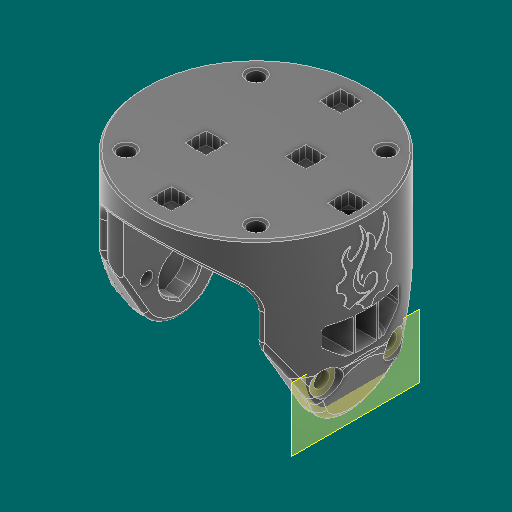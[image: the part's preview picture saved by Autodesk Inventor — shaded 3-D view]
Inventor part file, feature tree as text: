
AUTODESK INVENTOR PART (.ipt)
format: ipt  version: 2023.1 (Build 271208000, 208)  size: 2,006,016 bytes
history: native  units: in
note: dims shown in document units (in); Inventor stores cm internally (conversion verified against a paired STEP export)
features: sketch x14, other x12, plane x5
ambient origin geometry x8: Origin, YZ Plane, XZ Plane, XY Plane, X Axis, Y Axis, Z Axis, Center Point
bodies: Solid5 (feature_tree)
feature tree (31):
  other  "Carriage_MIR.ipt"
  other  "Solid2::Carriage_MIR.ipt"
  other  "Solid6::Carriage_MIR.ipt"
  other  "Solid4::Carriage_MIR.ipt"
  other  "Solid5::Carriage_MIR.ipt"
  other  "TaggingFeature1"
  sketch  "Sketch2"  dims[d0=0.3937in]
  sketch  "Sketch3"
  sketch  "Sketch5"
  sketch  "Sketch11"
  sketch  "Sketch6"
  sketch  "Sketch7"
  sketch  "Sketch8"
  sketch  "Sketch9"
  sketch  "Sketch13"
  sketch  "Sketch14"
  sketch  "Sketch16"
  sketch  "Sketch17"
  sketch  "Sketch18"
  sketch  "Sketch19"
  plane  "Work Plane1"
  plane  "Work Plane3"
  plane  "Work Plane4"
  plane  "Work Plane5"
  plane  "Work Plane6"
  other  "Work Axis1"
  other  "Work Axis2"
  other  "Srf1"
  other  "Srf2"
  other  "Srf1::Derived"
  other  "Srf2::Derived"
